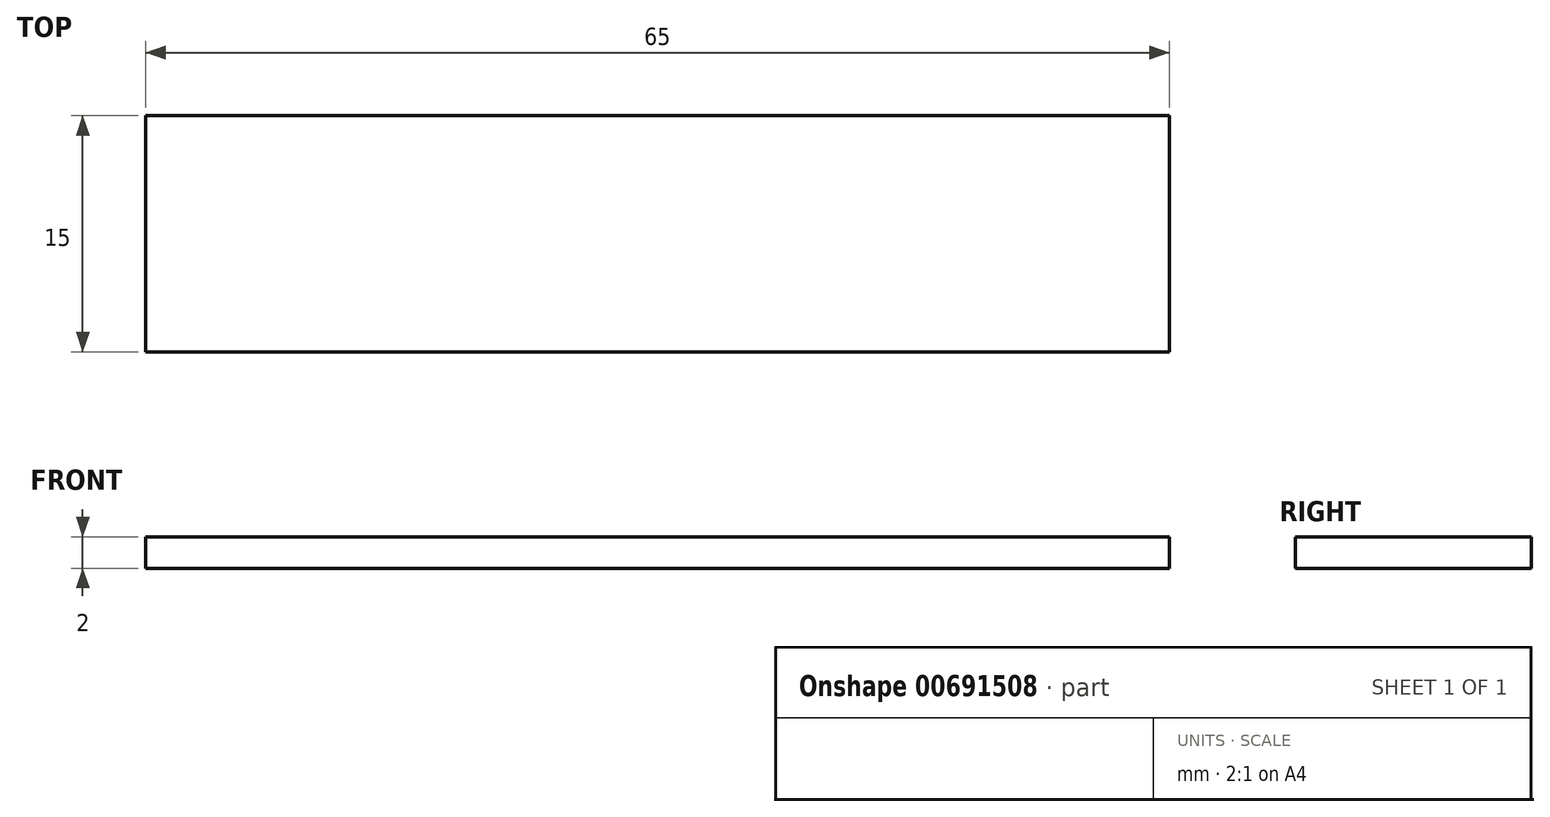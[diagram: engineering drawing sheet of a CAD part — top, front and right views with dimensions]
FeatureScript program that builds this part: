
annotation { "Feature Type Name" : "Feature", "Feature Type Description" : "" }
export const myFeature = defineFeature(function(context is Context, id is Id, definition is map)
    precondition{}
    {
        {
            var Q0;
            Q0=qCreatedBy(makeId("Top.planeOp"),FACE);
            var sketch = newSketch(context, id + "F0", { "sketchPlane" : qUnion([Q0])});
            skLineSegment(sketch, "E0.bottom", {"start": v(32.5, 7.5) * mm, "end": v(-32.5, 7.5) * mm});
            skLineSegment(sketch, "E0.top", {"start": v(32.5, -7.5) * mm, "end": v(-32.5, -7.5) * mm});
            skLineSegment(sketch, "E0.left", {"start": v(32.5, 7.5) * mm, "end": v(32.5, -7.5) * mm});
            skLineSegment(sketch, "E0.right", {"start": v(-32.5, 7.5) * mm, "end": v(-32.5, -7.5) * mm});
            skPoint(sketch, "E0.middle", {"position": v(0, 0) * mm});
            skSolve(sketch);
        }
        {
            var Q0;
            Q0 = qSketchRegion(id + "F0", true);
            extrude(context, id + "F1", {"entities" : qUnion([Q0]), "depth" : 2 * mm, "offsetDistance" : 25 * mm});
        }
    });
